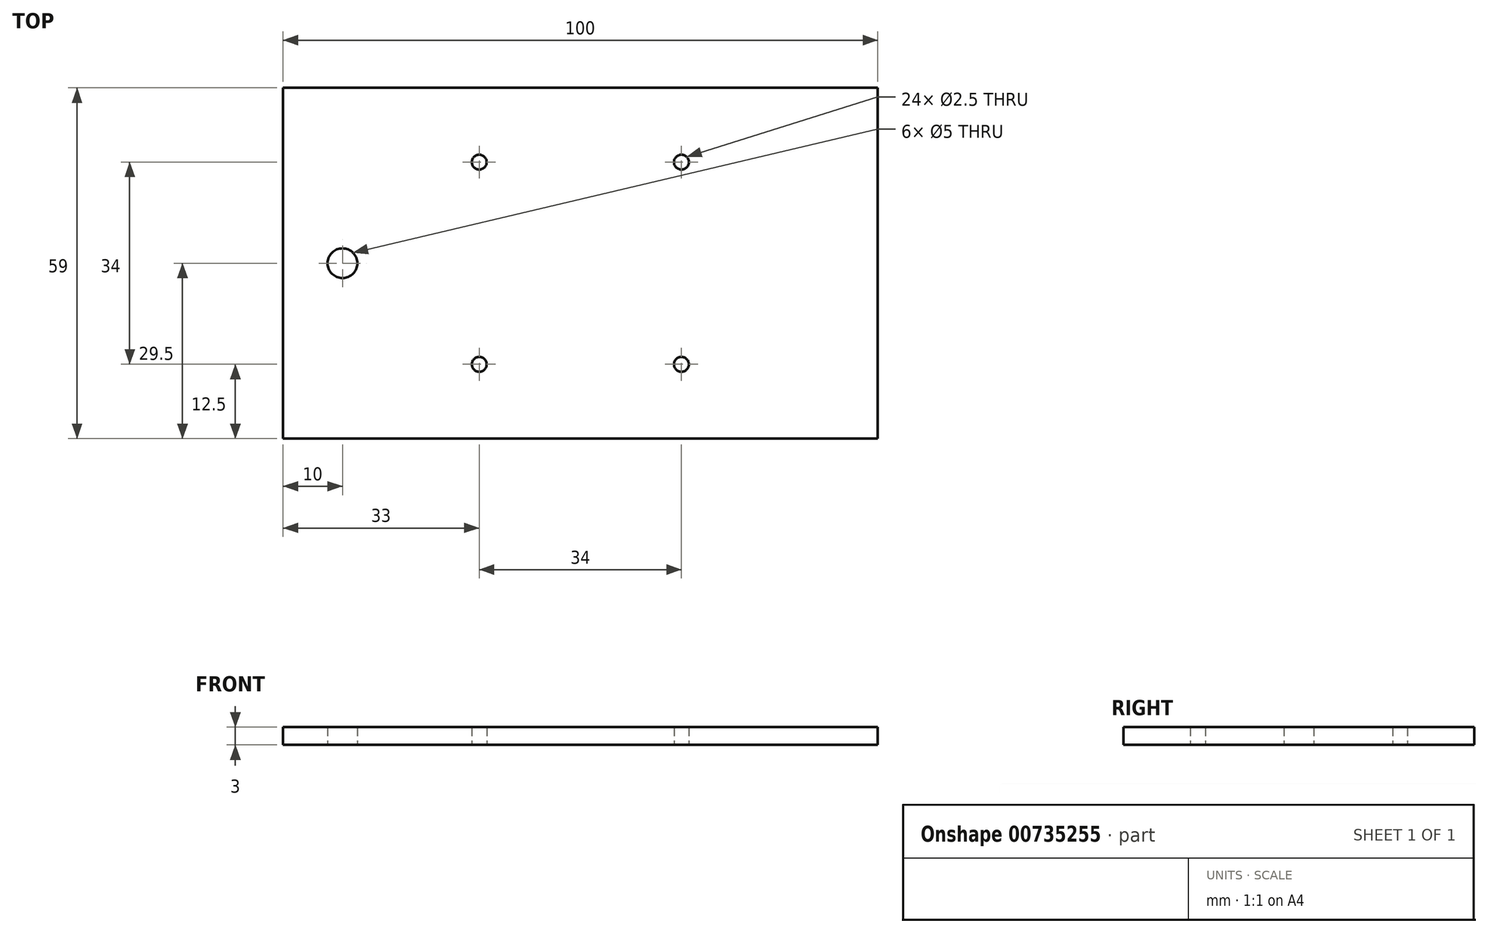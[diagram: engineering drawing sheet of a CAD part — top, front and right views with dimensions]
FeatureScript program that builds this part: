
annotation { "Feature Type Name" : "Feature", "Feature Type Description" : "" }
export const myFeature = defineFeature(function(context is Context, id is Id, definition is map)
    precondition{}
    {
        {
            var Q0;
            Q0=qCreatedBy(makeId("Top.planeOp"),FACE);
            var sketch = newSketch(context, id + "F0", { "sketchPlane" : qUnion([Q0])});
            skLineSegment(sketch, "E0.bottom", {"start": v(50, 29.5) * mm, "end": v(-50, 29.5) * mm});
            skLineSegment(sketch, "E0.top", {"start": v(50, -29.5) * mm, "end": v(-50, -29.5) * mm});
            skLineSegment(sketch, "E0.left", {"start": v(50, 29.5) * mm, "end": v(50, -29.5) * mm});
            skLineSegment(sketch, "E0.right", {"start": v(-50, 29.5) * mm, "end": v(-50, -29.5) * mm});
            skPoint(sketch, "E0.middle", {"position": v(0, 0) * mm});
            skCircle(sketch, "E1", {"center": v(17, 17) * mm, "radius": 1.25 * mm});
            skCircle(sketch, "E2", {"center": v(17, -17) * mm, "radius": 1.25 * mm});
            skCircle(sketch, "E3", {"center": v(-17, -17) * mm, "radius": 1.25 * mm});
            skCircle(sketch, "E4", {"center": v(-17, 17) * mm, "radius": 1.25 * mm});
            skCircle(sketch, "E5", {"center": v(-40, 0) * mm, "radius": 2.5 * mm});
            skSolve(sketch);
        }
        {
            var Q0;
            Q0=makeQuery(id+"F0.imprint","IMPRINT",FACE,{"disambiguationData":[TD([[makeQuery(id+"F0.imprint","IMPRINT",EDGE,{"derivedFrom":sQuery(id+"F0.wireOp",EDGE,"E0.bottom")}),1.0]])]});
            extrude(context, id + "F1", {"entities" : qUnion([Q0]), "depth" : 3 * mm, "offsetDistance" : 25 * mm});
        }
    });
